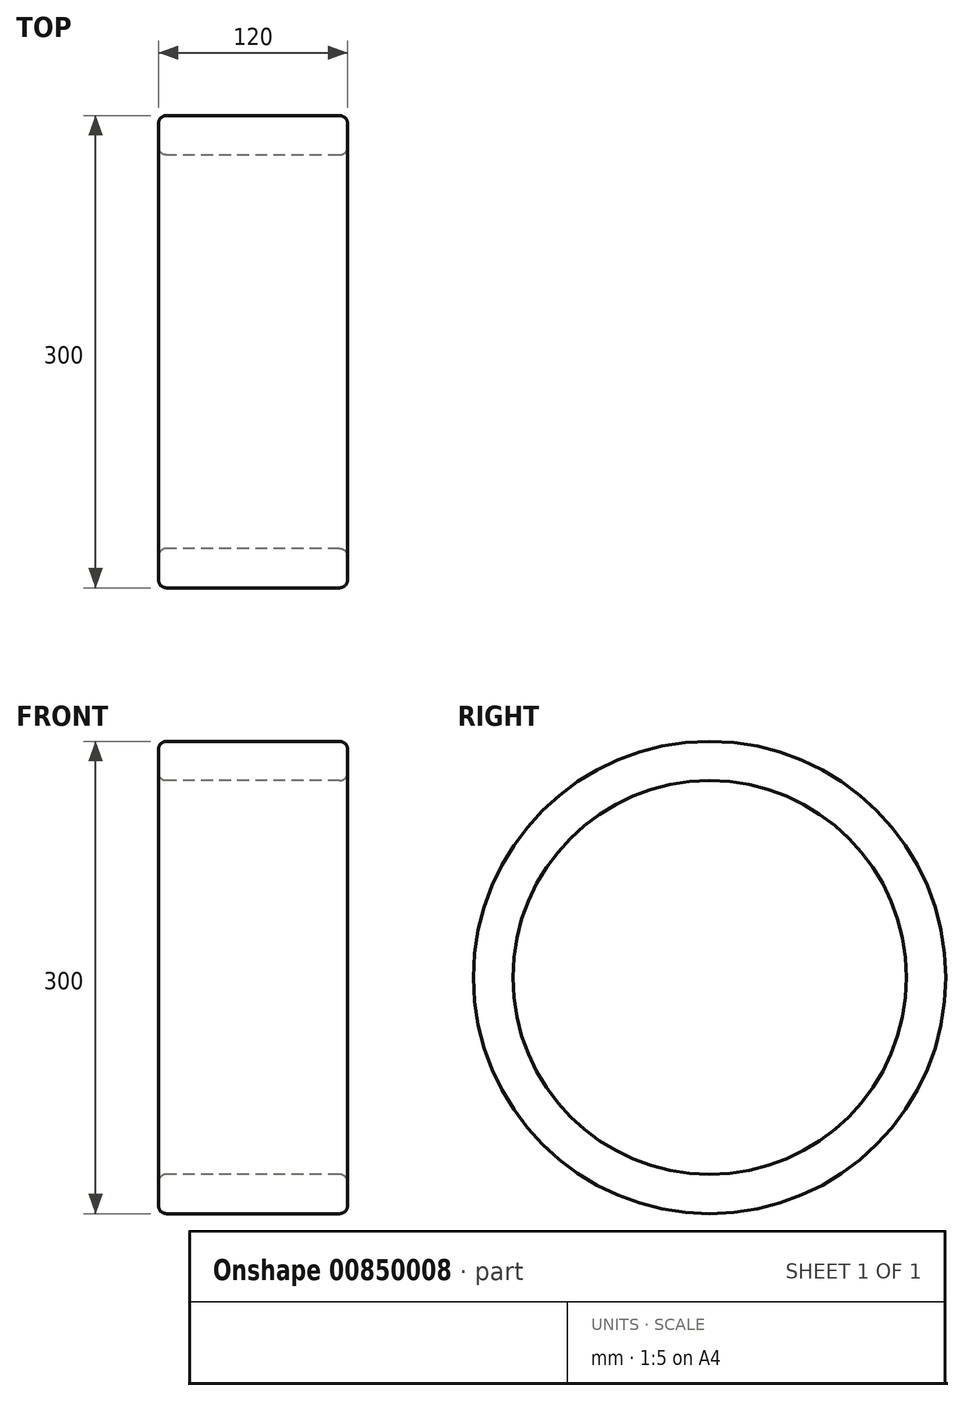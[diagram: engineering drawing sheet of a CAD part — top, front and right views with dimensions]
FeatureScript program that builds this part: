
annotation { "Feature Type Name" : "Feature", "Feature Type Description" : "" }
export const myFeature = defineFeature(function(context is Context, id is Id, definition is map)
    precondition{}
    {
        {
            var Q0;
            Q0=qCreatedBy(makeId("Right.planeOp"),FACE);
            var sketch = newSketch(context, id + "F0", { "sketchPlane" : qUnion([Q0])});
            skCircle(sketch, "E0", {"center": v(0, 0) * mm, "radius": 125 * mm});
            skCircle(sketch, "E1", {"center": v(0, 0) * mm, "radius": 150 * mm});
            skSolve(sketch);
        }
        {
            var Q0;
            Q0=makeQuery(id+"F0.imprint","IMPRINT",FACE,{"disambiguationData":[TD([[makeQuery(id+"F0.imprint","IMPRINT",EDGE,{"derivedFrom":sQuery(id+"F0.wireOp",EDGE,"E0")}),-1.0]])]});
            extrude(context, id + "F1", {"entities" : qUnion([Q0]), "depth" : 120 * mm, "offsetDistance" : 25 * mm});
        }
        {
            var Q0;
            Q0=makeQuery(id+"F1.opExtrude","CAP_EDGE",EDGE,{"disambiguationData":[OSD([sQuery(id+"F0.wireOp",EDGE,"E0")])],"isStart":false});
            var Q1;
            Q1=makeQuery(id+"F1.opExtrude","CAP_EDGE",EDGE,{"disambiguationData":[OSD([sQuery(id+"F0.wireOp",EDGE,"E1")])],"isStart":false});
            var Q2;
            Q2=makeQuery(id+"F1.opExtrude","CAP_EDGE",EDGE,{"disambiguationData":[OSD([sQuery(id+"F0.wireOp",EDGE,"E1")])],"isStart":true});
            var Q3;
            Q3=makeQuery(id+"F1.opExtrude","CAP_EDGE",EDGE,{"disambiguationData":[OSD([sQuery(id+"F0.wireOp",EDGE,"E0")])],"isStart":true});
            fillet(context, id + "F2", {"entities" : qUnion([Q0, Q1, Q2, Q3]), "radius" : 5 * mm, "tangentPropagation" : true, "allowEdgeOverflow" : false});
        }
    });
